FCSTD DOCUMENT  (FreeCAD 0.19R0.19.2)
Label: boatMoterHolder006
License: All rights reserved
LicenseURL: http://en.wikipedia.org/wiki/All_rights_reserved
objects: Sketcher::SketchObject×1
note: 1 computed .brp shape members not serialized (recipe doc carries the construction recipe); baked Part::Feature solids carry a one-line shape summary decoded from their .brp

FEATURE [Sketcher::SketchObject] Sketch
  FullyConstrained = true
  sketch-geometry (44):
    g0: Circle CenterX=-6 CenterY=0 CenterZ=0 NormalX=0 NormalY=0 NormalZ=1 AngleXU=0 Radius=0.9
    g1: Circle CenterX=0 CenterY=6 CenterZ=0 NormalX=0 NormalY=0 NormalZ=1 AngleXU=0 Radius=0.9
    g2: Circle CenterX=6 CenterY=0 CenterZ=0 NormalX=0 NormalY=0 NormalZ=1 AngleXU=0 Radius=0.9
    g3: Circle CenterX=0 CenterY=-6 CenterZ=0 NormalX=0 NormalY=0 NormalZ=1 AngleXU=0 Radius=0.9
    g4-g8: Circle x5 (B-spline internal-alignment scaffolding for g9; pole/knot coordinates omitted)
    g9: BSplineCurve PolesCount=5 KnotsCount=3 Degree=3 IsPeriodic=0
    g10: GeomPoint X=-4.94974 Y=10.6066 Z=0
    g11: GeomPoint X=-4.24264 Y=4.24264 Z=0
    g12: GeomPoint X=-10.6066 Y=4.94975 Z=0
    g13-g17: Circle x5 (B-spline internal-alignment scaffolding for g18; pole/knot coordinates omitted)
    g18: BSplineCurve PolesCount=5 KnotsCount=3 Degree=3 IsPeriodic=0
    g19: GeomPoint X=-10.6066 Y=-4.94974 Z=0
    g20: GeomPoint X=-4.23566 Y=-4.23553 Z=0
    g21: GeomPoint X=-4.94053 Y=-10.6109 Z=0
    g22-g26: Circle x5 (B-spline internal-alignment scaffolding for g27; pole/knot coordinates omitted)
    g27: BSplineCurve PolesCount=5 KnotsCount=3 Degree=3 IsPeriodic=0
    g28: GeomPoint X=4.94975 Y=-10.6066 Z=0
    g29: GeomPoint X=4.23876 Y=-4.2388 Z=0
    g30: GeomPoint X=10.603 Y=-4.95737 Z=0
    g31-g35: Circle x5 (B-spline internal-alignment scaffolding for g36; pole/knot coordinates omitted)
    g36: BSplineCurve PolesCount=5 KnotsCount=3 Degree=3 IsPeriodic=0
    g37: GeomPoint X=10.6066 Y=4.94975 Z=0
    g38: GeomPoint X=4.24264 Y=4.24264 Z=0
    g39: GeomPoint X=4.94975 Y=10.6066 Z=0
    g40: ArcOfCircle CenterX=0 CenterY=0 CenterZ=0 NormalX=0 NormalY=0 NormalZ=1 AngleXU=0 Radius=11.7047 StartAngle=1.13417 EndAngle=2.00742
    g41: ArcOfCircle CenterX=0 CenterY=0 CenterZ=0 NormalX=0 NormalY=0 NormalZ=1 AngleXU=0 Radius=11.7047 StartAngle=5.84584 EndAngle=6.71981
    g42: ArcOfCircle CenterX=0 CenterY=0 CenterZ=0 NormalX=0 NormalY=0 NormalZ=1 AngleXU=0 Radius=11.7047 StartAngle=4.27663 EndAngle=5.14902
    g43: ArcOfCircle CenterX=0 CenterY=0 CenterZ=0 NormalX=0 NormalY=0 NormalZ=1 AngleXU=0 Radius=11.7047 StartAngle=2.70497 EndAngle=3.57822
  constraints (50):
    c: Block(g1)
    c: Block(g2)
    c: Block(g3)
    c: Block(g0)
    c: Weight(g4) = 1
    c: Equal(g4, g5-g8) x4
    c: InternalAlignment(g4-g8 -> g9) x5
    c: InternalAlignment(g10,g9)
    c: InternalAlignment(g11,g9)
    c: InternalAlignment(g12,g9)
    c: Weight(g13) = 1
    c: Equal(g13, g14-g17) x4
    c: InternalAlignment(g13-g17 -> g18) x5
    c: InternalAlignment(g19,g18)
    c: InternalAlignment(g20,g18)
    c: InternalAlignment(g21,g18)
    c: Weight(g22) = 1
    c: Equal(g22,g24)
    c: Equal(g22,g25)
    c: Equal(g22,g26)
    c: InternalAlignment(g22-g26 -> g27) x5
    c: InternalAlignment(g28,g27)
    c: InternalAlignment(g29,g27)
    c: InternalAlignment(g30,g27)
    c: Weight(g31) = 1
    c: Equal(g31, g32-g35) x4
    c: InternalAlignment(g31-g35 -> g36) x5
    c: InternalAlignment(g37,g36)
    c: InternalAlignment(g38,g36)
    c: InternalAlignment(g39,g36)
    c: Coincident(g40,g-1)
    c: Coincident(g40,g9)
    c: Coincident(g40,g36)
    c: Coincident(g41,g40)
    c: Coincident(g41,g36)
    c: Coincident(g41,g27)
    c: Coincident(g42,g40)
    c: Coincident(g42,g27)
    c: Coincident(g42,g18)
    c: Coincident(g43,g40)
    c: Coincident(g43,g18)
    c: Coincident(g43,g9)
    c: Block(g41)
    c: Block(g36)
    c: Block(g27)
    c: Block(g40)
    c: Block(g9)
    c: Block(g43)
    c: Block(g18)
    c: Block(g42)
